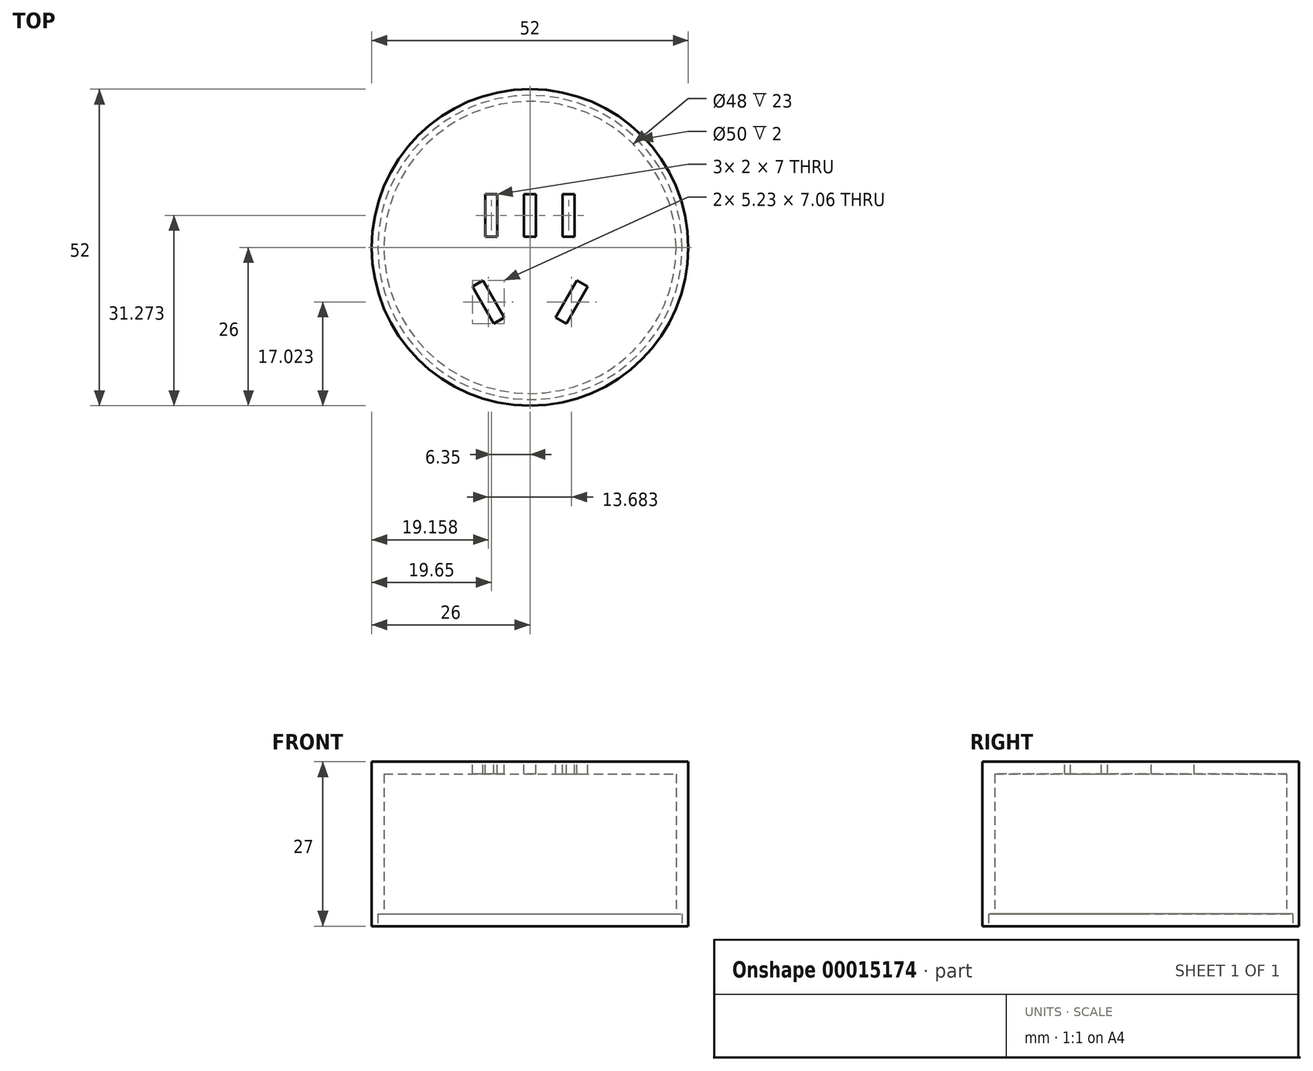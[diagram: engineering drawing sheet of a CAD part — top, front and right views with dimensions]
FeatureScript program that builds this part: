
annotation { "Feature Type Name" : "Feature", "Feature Type Description" : "" }
export const myFeature = defineFeature(function(context is Context, id is Id, definition is map)
    precondition{}
    {
        {
            var Q0;
            Q0=qCreatedBy(makeId("Top.planeOp"),FACE);
            var sketch = newSketch(context, id + "F0", { "sketchPlane" : qUnion([Q0])});
            skCircle(sketch, "E0", {"center": v(0, 0) * mm, "radius": 26 * mm});
            skSolve(sketch);
        }
        {
            var Q0;
            Q0=makeQuery(id+"F0.imprint","IMPRINT",FACE,{"disambiguationData":[TD([[makeQuery(id+"F0.imprint","IMPRINT",EDGE,{"derivedFrom":sQuery(id+"F0.wireOp",EDGE,"E0")}),1.0]])]});
            extrude(context, id + "F1", {"entities" : qUnion([Q0]), "depth" : 27 * mm});
        }
        {
            var Q0;
            Q0=makeQuery(id+"F1.opExtrude","CAP_FACE",FACE,{"disambiguationData":[OSD([sQuery(id+"F0.wireOp",EDGE,"E0")])],"isStart":false});
            var sketch = newSketch(context, id + "F2", { "sketchPlane" : qUnion([Q0])});
            skLineSegment(sketch, "E1", {"start": v(0, 26) * mm, "end": v(0, -26) * mm, "construction": true});
            skLineSegment(sketch, "E2", {"start": v(0, -5.03) * mm, "end": v(-20.02, -16.59) * mm, "construction": true});
            skLineSegment(sketch, "E3", {"start": v(0, -5.03) * mm, "end": v(20.02, -16.59) * mm, "construction": true});
            skLineSegment(sketch, "E4.rect.bottom", {"start": v(1, 1.77) * mm, "end": v(-1, 1.77) * mm});
            skLineSegment(sketch, "E4.rect.top", {"start": v(1, 8.77) * mm, "end": v(-1, 8.77) * mm});
            skLineSegment(sketch, "E4.rect.left", {"start": v(1, 1.77) * mm, "end": v(1, 8.77) * mm});
            skLineSegment(sketch, "E4.rect.right", {"start": v(-1, 1.77) * mm, "end": v(-1, 8.77) * mm});
            skPoint(sketch, "E4.rect.middle", {"position": v(0, 5.27) * mm});
            skLineSegment(sketch, "E5", {"start": v(0, 5.27) * mm, "end": v(-25.46, 5.27) * mm, "construction": true});
            skLineSegment(sketch, "E6.rect.bottom", {"start": v(-5.35, 1.77) * mm, "end": v(-7.35, 1.77) * mm});
            skLineSegment(sketch, "E6.rect.top", {"start": v(-5.35, 8.77) * mm, "end": v(-7.35, 8.77) * mm});
            skLineSegment(sketch, "E6.rect.left", {"start": v(-5.35, 1.77) * mm, "end": v(-5.35, 8.77) * mm});
            skLineSegment(sketch, "E6.rect.right", {"start": v(-7.35, 1.77) * mm, "end": v(-7.35, 8.77) * mm});
            skPoint(sketch, "E6.rect.middle", {"position": v(-6.35, 5.27) * mm});
            skLineSegment(sketch, "E7.rect.bottom", {"start": v(-4.23, -11.5) * mm, "end": v(-5.96, -12.5) * mm});
            skLineSegment(sketch, "E7.rect.top", {"start": v(-7.73, -5.45) * mm, "end": v(-9.46, -6.45) * mm});
            skLineSegment(sketch, "E7.rect.left", {"start": v(-4.23, -11.5) * mm, "end": v(-7.73, -5.45) * mm});
            skLineSegment(sketch, "E7.rect.right", {"start": v(-5.96, -12.5) * mm, "end": v(-9.46, -6.45) * mm});
            skPoint(sketch, "E7.rect.middle", {"position": v(-6.84, -8.98) * mm});
            skLineSegment(sketch, "E8.rect.bottom", {"start": v(4.23, -11.5) * mm, "end": v(7.73, -5.45) * mm});
            skLineSegment(sketch, "E8.rect.top", {"start": v(5.96, -12.5) * mm, "end": v(9.46, -6.45) * mm});
            skLineSegment(sketch, "E8.rect.left", {"start": v(4.23, -11.5) * mm, "end": v(5.96, -12.5) * mm});
            skLineSegment(sketch, "E8.rect.right", {"start": v(7.73, -5.45) * mm, "end": v(9.46, -6.45) * mm});
            skPoint(sketch, "E8.rect.middle", {"position": v(6.84, -8.98) * mm});
            skLineSegment(sketch, "E9.MirrorCS", {"start": v(5.35, 1.77) * mm, "end": v(7.35, 1.77) * mm});
            skLineSegment(sketch, "E10.MirrorCS", {"start": v(5.35, 8.77) * mm, "end": v(7.35, 8.77) * mm});
            skLineSegment(sketch, "E11.MirrorCS", {"start": v(7.35, 1.77) * mm, "end": v(7.35, 8.77) * mm});
            skLineSegment(sketch, "E12.MirrorCS", {"start": v(5.35, 1.77) * mm, "end": v(5.35, 8.77) * mm});
            skCircle(sketch, "E13", {"center": v(0, 0) * mm, "radius": 11.45 * mm, "construction": true});
            skSolve(sketch);
        }
        {
            var Q0;
            Q0=makeQuery(id+"F2.imprint","IMPRINT",FACE,{"disambiguationData":[TD([[makeQuery(id+"F2.imprint","IMPRINT",EDGE,{"derivedFrom":sQuery(id+"F2.wireOp",EDGE,"E6.rect.bottom")}),-1.0]])]});
            var Q1;
            Q1=makeQuery(id+"F2.imprint","IMPRINT",FACE,{"disambiguationData":[TD([[makeQuery(id+"F2.imprint","IMPRINT",EDGE,{"derivedFrom":sQuery(id+"F2.wireOp",EDGE,"E4.rect.bottom")}),-1.0]])]});
            var Q2;
            Q2=makeQuery(id+"F2.imprint","IMPRINT",FACE,{"disambiguationData":[TD([[makeQuery(id+"F2.imprint","IMPRINT",EDGE,{"derivedFrom":sQuery(id+"F2.wireOp",EDGE,"E9.MirrorCS")}),1.0]])]});
            var Q3;
            Q3=makeQuery(id+"F2.imprint","IMPRINT",FACE,{"disambiguationData":[TD([[makeQuery(id+"F2.imprint","IMPRINT",EDGE,{"derivedFrom":sQuery(id+"F2.wireOp",EDGE,"E8.rect.bottom")}),-1.0]])]});
            var Q4;
            Q4=makeQuery(id+"F2.imprint","IMPRINT",FACE,{"disambiguationData":[TD([[makeQuery(id+"F2.imprint","IMPRINT",EDGE,{"derivedFrom":sQuery(id+"F2.wireOp",EDGE,"E7.rect.bottom")}),-1.0]])]});
            extrude(context, id + "F3", {"entities" : qUnion([Q0, Q1, Q2, Q3, Q4]), "operationType" : NewBodyOperationType.REMOVE, "endBound" : BoundingType.THROUGH_ALL, "oppositeDirection" : true, "depth" : 23 * mm});
        }
        {
            var Q0;
            Q0=makeQuery(id+"F1.opExtrude","CAP_FACE",FACE,{"disambiguationData":[OSD([sQuery(id+"F0.wireOp",EDGE,"E0")])],"isStart":true});
            var sketch = newSketch(context, id + "F4", { "sketchPlane" : qUnion([Q0])});
            skCircle(sketch, "E14", {"center": v(0, 0) * mm, "radius": 24 * mm});
            skSolve(sketch);
        }
        {
            var Q0;
            Q0=makeQuery(id+"F4.imprint","IMPRINT",FACE,{"disambiguationData":[TD([[makeQuery(id+"F4.imprint","IMPRINT",EDGE,{"derivedFrom":sQuery(id+"F4.wireOp",EDGE,"E14")}),1.0]])]});
            extrude(context, id + "F5", {"entities" : qUnion([Q0]), "operationType" : NewBodyOperationType.REMOVE, "oppositeDirection" : true, "depth" : 25 * mm});
        }
        {
            var Q0;
            Q0=makeQuery(id+"F1.opExtrude","CAP_FACE",FACE,{"disambiguationData":[OSD([sQuery(id+"F0.wireOp",EDGE,"E0")])],"isStart":true});
            var sketch = newSketch(context, id + "F6", { "sketchPlane" : qUnion([Q0])});
            skCircle(sketch, "E15", {"center": v(0, 0) * mm, "radius": 25 * mm});
            skSolve(sketch);
        }
        {
            var Q0;
            Q0 = qSketchRegion(id + "F6", true);
            extrude(context, id + "F7", {"entities" : qUnion([Q0]), "operationType" : NewBodyOperationType.REMOVE, "oppositeDirection" : true, "depth" : 2 * mm});
        }
    });
